# Revit family: ROTHOB_Rothoblaas_FallProtection_BLOCK
name_source: partatom
category: Specialty Equipment
units: mm (PartAtom-declared; Revit-internal decimal feet)

## family parameters
Cut with Voids When Loaded = No
Host = Face
Maintain Annotation Orientation = No
OmniClass Number = 23.27.71.21
Part Type = Normal
Room Calculation Point = No
Round Connector Dimension = Use Diameter
Shared = No

## types (3) — shared parameters
AssetType = Fixed
BIMObjectName = ROTHOB_Rothoblaas_FallProtection_BLOCK
Category = Pr_40_70_75_75 - Safety access anchor devices
CodePerformance = CE - Safety system
Color = Grey
Default Elevation = 1219.2 mm  [stored 4 ft]
Description = Support with ballast for fall protection systems for non-drillable green roofs and flat roofs (slope up to 5°)
DurationUnit = Years
Esporta tipo in formato IFC con nome = IfcBuildingElementProxyType
Features = Horizontal lifeline and anchor points
Finish = Stainless steel
IfcElementType = FALL_ARRESTER_DEVICES
IfcExportAs = IfcBuildingElementProxyType
IfcExportType = USERDEFINED
Lenght_L = 1891.24 mm
ManufacturerName = ROTHO BLAAS SRL
ManufacturerURL = www.rothoblaas.com
Material = AISI 304 stainless steel grade 1.4301
MinWeight = BLOCK 19.3 kg / BLOCK with 18 ballasts 400 kg
ModelDisclaimer = The latest version of the data sheets can be found on our website // BLOCKMAT, BLOCKPLATE and Ballasts are not included with the purchase of BLOCK
ModelNumber = BLOCK
Name = Support for fall protection systems
NominalLength = 1891.24 mm
NominalWidth = 1668.53 mm
ObjectMaterial = ROTHOB_Rothoblaas_StainlessSteelAISI304
OmniClassCode = 23-27 71 21
OmniClassTitle = Fall Arrest Systems
OmniClassVersion = 2012-05-16
ProductInformation = https://www.rothoblaas.com
ReferenceStandard = with PATROL: EN 795:2012 C | CEN/TS 16415:2013 | UNI 11578:2015 C //  with AOS01: EN 795:2012 E
Revision = 001
Shape = Three-dimensional
Size = 1891x1669x210 mm
Tipo IFC predefinito = USERDEFINED
UniClass2015Code = Pr_40_70_75_75
UniClass2015Title = Safety access anchor devices
UniClass2015Version = Products v1.38
Version = 001
Width_B = 1668.53 mm

## per-type parameters (varying)
| type | BLOCKMAT | BLOCKPLATE | GTIN | H_BLOCKMAT | Height_H | NominalHeight | N°Ballast=24 |
| BLOCK+BLOCKMAT_1891x1669x210mm | Yes | No | BLOCK: 8052877750641 / BLOCKMAT: 8052877751068 | 6 mm  [stored 0.019685 ft] | 165.5 mm  [stored 0.542979 ft] | 165.5 mm  [stored 0.542979 ft] | Yes |
| BLOCK+BLOCKMAT+BLOCKPLATE_1891x1669x210mm | Yes | Yes | BLOCK: 8052877750641 / BLOCKMAT: 8052877751068 / BLOCKPLATE: 8054045435831 | 6 mm  [stored 0.019685 ft] | 209.5 mm | 209.5 mm | No |
| BLOCK+BLOCKPLATE_1891x1669x210mm | No | Yes | BLOCK: 8052877750641 / BLOCKPLATE: 8054045435831 | 0 mm  [stored 0 ft] | 165.5 mm  [stored 0.542979 ft] | 165.5 mm  [stored 0.542979 ft] | No |

note: [stored X ft] marks values corroborated as IEEE doubles in the binary element streams (Revit-internal decimal feet)

## geometry (parser evidence)
native form markers: Sweep x25
no freeform markers — native parametric forms only
